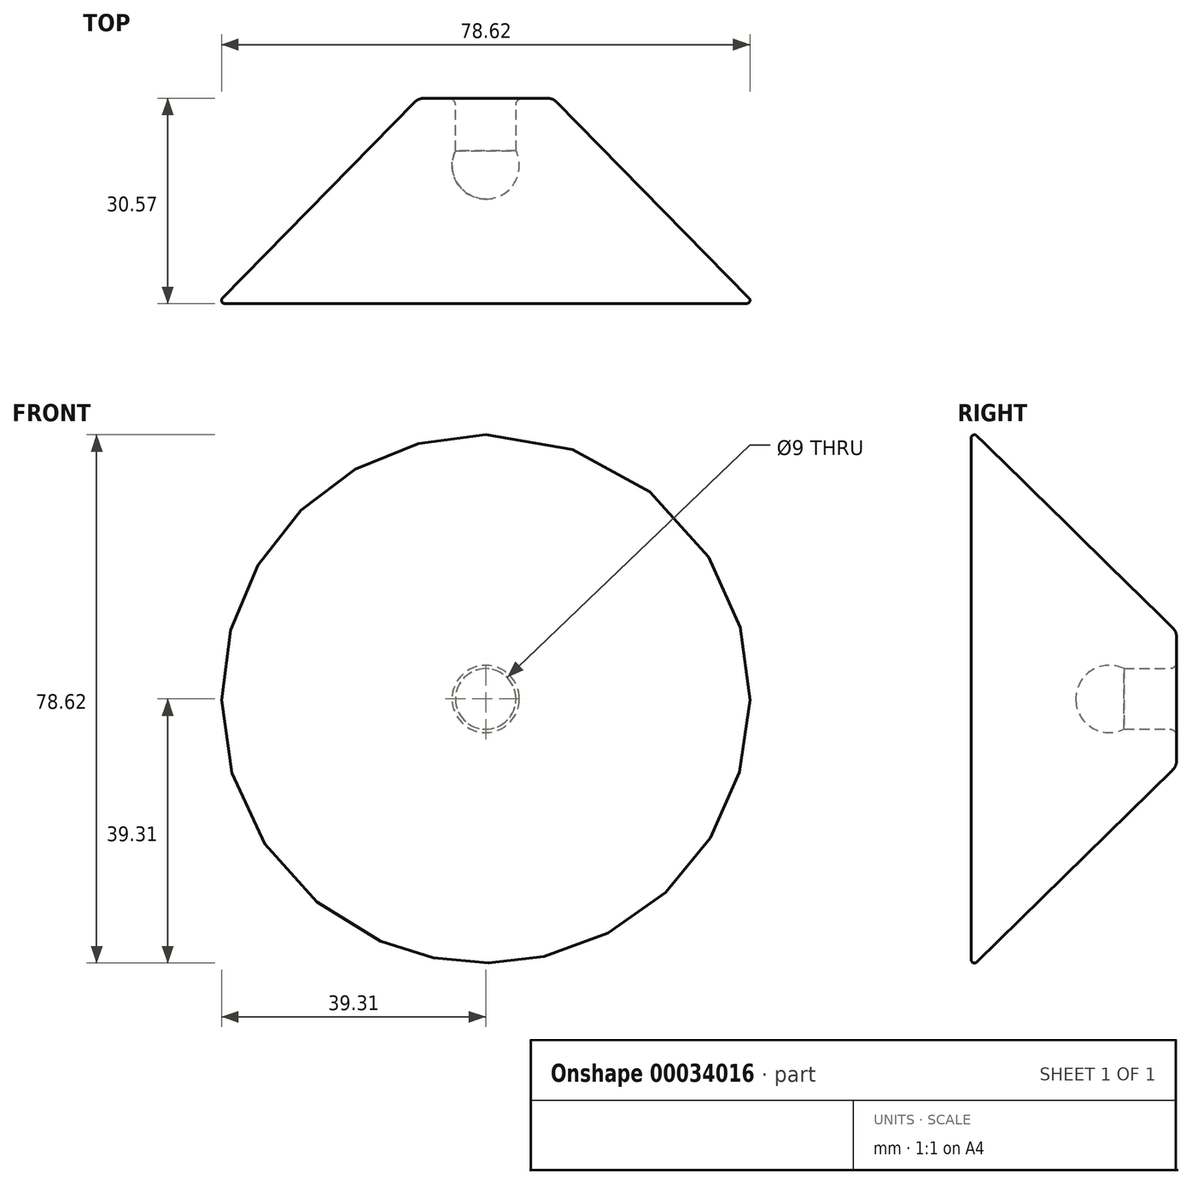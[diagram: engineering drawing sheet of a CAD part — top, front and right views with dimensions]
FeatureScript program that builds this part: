
annotation { "Feature Type Name" : "Feature", "Feature Type Description" : "" }
export const myFeature = defineFeature(function(context is Context, id is Id, definition is map)
    precondition{}
    {
        {
            var Q0;
            Q0=qCreatedBy(makeId("Top.planeOp"),FACE);
            var sketch = newSketch(context, id + "F0", { "sketchPlane" : qUnion([Q0])});
            skLineSegment(sketch, "E0", {"start": v(-39.17, 0.85) * mm, "end": v(-10.59, 29.97) * mm});
            skLineSegment(sketch, "E1", {"start": v(-9.16, 30.57) * mm, "end": v(-5.5, 30.57) * mm});
            skLineSegment(sketch, "E2", {"start": v(-4.5, 29.57) * mm, "end": v(-4.5, 22.75) * mm});
            skLineSegment(sketch, "E3", {"start": v(-4.5, 0) * mm, "end": v(-38.8, 0) * mm});
            skArc(sketch, "E4", {"start": v(-4.5, 22.75) * mm, "mid": v(-4.24, 17.91) * mm, "end": v(0, 15.57) * mm});
            skLineSegment(sketch, "E5", {"start": v(0, 0) * mm, "end": v(-4.5, 0) * mm});
            skLineSegment(sketch, "E6", {"start": v(0, 15.57) * mm, "end": v(0, 0) * mm});
            skPoint(sketch, "E7.visualSharp", {"position": v(-40, 0) * mm});
            skArc(sketch, "E7.filletArc", {"start": v(-39.17, 0.85) * mm, "mid": v(-39.27, 0.3) * mm, "end": v(-38.8, 0) * mm});
            skPoint(sketch, "E8.visualSharp", {"position": v(-10, 30.57) * mm});
            skArc(sketch, "E8.filletArc", {"start": v(-9.16, 30.57) * mm, "mid": v(-9.93, 30.41) * mm, "end": v(-10.59, 29.97) * mm});
            skPoint(sketch, "E9.visualSharp", {"position": v(-4.5, 30.57) * mm});
            skArc(sketch, "E9.filletArc", {"start": v(-4.5, 29.57) * mm, "mid": v(-4.8, 30.28) * mm, "end": v(-5.5, 30.57) * mm});
            skSolve(sketch);
        }
        {
            var Q0;
            Q0=makeQuery(id+"F0.imprint","IMPRINT",FACE,{"disambiguationData":[TD([[makeQuery(id+"F0.imprint","IMPRINT",EDGE,{"derivedFrom":sQuery(id+"F0.wireOp",EDGE,"E0")}),-1.0]])]});
            var Q1;
            Q1=sQuery(id+"F0.wireOp",EDGE,"E6");
            revolve(context, id + "F1", {"entities" : qUnion([Q0]), "axis" : qUnion([Q1]), "revolveType" : RevolveType.FULL});
        }
    });
